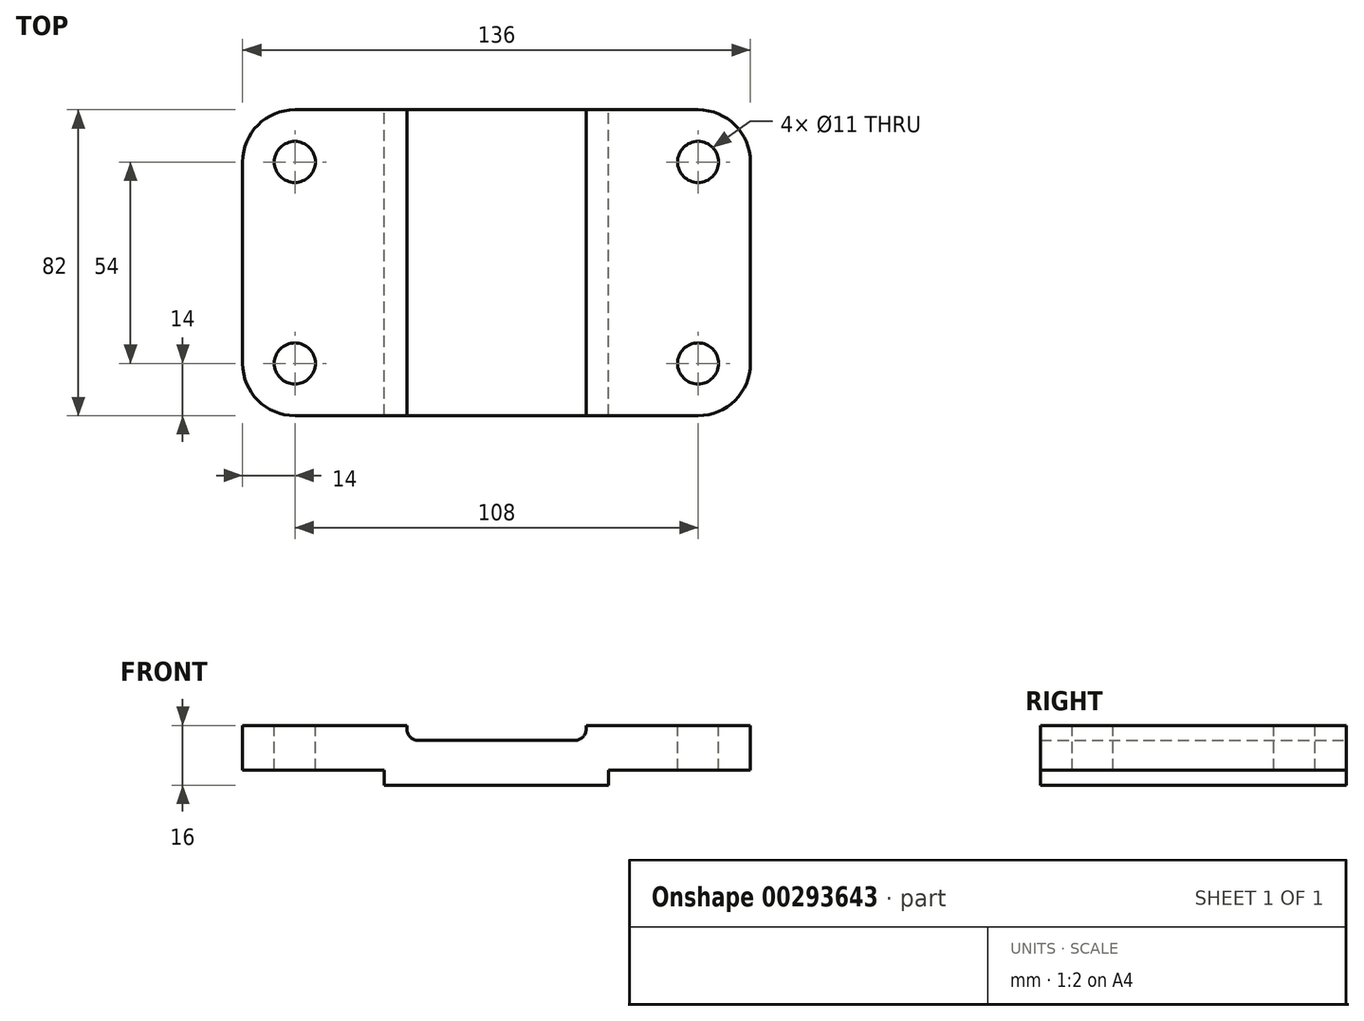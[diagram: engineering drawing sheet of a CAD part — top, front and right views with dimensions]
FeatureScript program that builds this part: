
annotation { "Feature Type Name" : "Feature", "Feature Type Description" : "" }
export const myFeature = defineFeature(function(context is Context, id is Id, definition is map)
    precondition{}
    {
        {
            var Q0;
            Q0=qCreatedBy(makeId("Front.planeOp"),FACE);
            var sketch = newSketch(context, id + "F0", { "sketchPlane" : qUnion([Q0])});
            skLineSegment(sketch, "E0", {"start": v(0, 0) * mm, "end": v(0, 4) * mm});
            skLineSegment(sketch, "E1", {"start": v(0, 4) * mm, "end": v(-38, 4) * mm});
            skLineSegment(sketch, "E2", {"start": v(-38, 4) * mm, "end": v(-38, 16) * mm});
            skLineSegment(sketch, "E3", {"start": v(-38, 16) * mm, "end": v(6, 16) * mm});
            skLineSegment(sketch, "E4", {"start": v(6, 16) * mm, "end": v(6, 15) * mm});
            skLineSegment(sketch, "E5", {"start": v(9, 12) * mm, "end": v(51, 12) * mm});
            skLineSegment(sketch, "E6", {"start": v(54, 15) * mm, "end": v(54, 16) * mm});
            skLineSegment(sketch, "E7", {"start": v(54, 16) * mm, "end": v(98, 16) * mm});
            skLineSegment(sketch, "E8", {"start": v(98, 16) * mm, "end": v(98, 4) * mm});
            skLineSegment(sketch, "E9", {"start": v(98, 4) * mm, "end": v(60, 4) * mm});
            skLineSegment(sketch, "E10", {"start": v(60, 4) * mm, "end": v(60, 0) * mm});
            skLineSegment(sketch, "E11", {"start": v(60, 0) * mm, "end": v(0, 0) * mm});
            skPoint(sketch, "E12.visualSharp", {"position": v(6, 12) * mm});
            skArc(sketch, "E12.filletArc", {"start": v(6, 15) * mm, "mid": v(6.88, 12.88) * mm, "end": v(9, 12) * mm});
            skPoint(sketch, "E13.visualSharp", {"position": v(54, 12) * mm});
            skArc(sketch, "E13.filletArc", {"start": v(51, 12) * mm, "mid": v(53.12, 12.88) * mm, "end": v(54, 15) * mm});
            skSolve(sketch);
        }
        {
            var Q0;
            Q0=makeQuery(id+"F0.imprint","IMPRINT",FACE,{"disambiguationData":[TD([[makeQuery(id+"F0.imprint","IMPRINT",EDGE,{"derivedFrom":sQuery(id+"F0.wireOp",EDGE,"E0")}),-1.0]])]});
            extrude(context, id + "F1", {"entities" : qUnion([Q0]), "depth" : 82 * mm});
        }
        {
            var Q0;
            Q0=makeQuery(id+"F1.opExtrude","CAP_EDGE",EDGE,{"disambiguationData":[OSD([sQuery(id+"F0.wireOp",EDGE,"E8")])],"isStart":false});
            var Q1;
            Q1=makeQuery(id+"F1.opExtrude","CAP_EDGE",EDGE,{"disambiguationData":[OSD([sQuery(id+"F0.wireOp",EDGE,"E8")])],"isStart":true});
            var Q2;
            Q2=makeQuery(id+"F1.opExtrude","CAP_EDGE",EDGE,{"disambiguationData":[OSD([sQuery(id+"F0.wireOp",EDGE,"E2")])],"isStart":true});
            var Q3;
            Q3=makeQuery(id+"F1.opExtrude","CAP_EDGE",EDGE,{"disambiguationData":[OSD([sQuery(id+"F0.wireOp",EDGE,"E2")])],"isStart":false});
            fillet(context, id + "F2", {"entities" : qUnion([Q0, Q1, Q2, Q3]), "radius" : 14 * mm, "tangentPropagation" : true, "allowEdgeOverflow" : false});
        }
        {
            var Q0;
            Q0=makeQuery(id+"F1.opExtrude","SWEPT_FACE",FACE,{"disambiguationData":[OSD([sQuery(id+"F0.wireOp",EDGE,"E3")])]});
            var sketch = newSketch(context, id + "F3", { "sketchPlane" : qUnion([Q0])});
            skLineSegment(sketch, "E14.0.0", {"start": v(6, 0) * mm, "end": v(-24, 0) * mm});
            skArc(sketch, "E14.0.1", {"start": v(-24, 0) * mm, "mid": v(-33.9, -4.1) * mm, "end": v(-38, -14) * mm});
            skLineSegment(sketch, "E14.0.2", {"start": v(-38, -14) * mm, "end": v(-38, -68) * mm});
            skArc(sketch, "E14.0.3", {"start": v(-38, -68) * mm, "mid": v(-33.9, -77.9) * mm, "end": v(-24, -82) * mm});
            skLineSegment(sketch, "E14.0.4", {"start": v(-24, -82) * mm, "end": v(6, -82) * mm});
            skLineSegment(sketch, "E14.0.5", {"start": v(6, -82) * mm, "end": v(6, 0) * mm});
            skCircle(sketch, "E15", {"center": v(-24, -14) * mm, "radius": 5.5 * mm});
            skCircle(sketch, "E16.0.1.0", {"center": v(-24, -68) * mm, "radius": 5.5 * mm});
            skCircle(sketch, "E16.1.0.0", {"center": v(84, -14) * mm, "radius": 5.5 * mm});
            skCircle(sketch, "E16.1.1.0", {"center": v(84, -68) * mm, "radius": 5.5 * mm});
            skLineSegment(sketch, "E16.direction1", {"start": v(-24, -14) * mm, "end": v(84, -14) * mm, "construction": true});
            skLineSegment(sketch, "E16.direction2", {"start": v(-24, -14) * mm, "end": v(-24, -68) * mm, "construction": true});
            skSolve(sketch);
        }
        {
            var Q0;
            Q0=makeQuery(id+"F3.imprint","IMPRINT",FACE,{"disambiguationData":[TD([[makeQuery(id+"F3.imprint","IMPRINT",EDGE,{"derivedFrom":sQuery(id+"F3.wireOp",EDGE,"E15")}),1.0]])]});
            var Q1;
            Q1=makeQuery(id+"F3.imprint","IMPRINT",FACE,{"disambiguationData":[TD([[makeQuery(id+"F3.imprint","IMPRINT",EDGE,{"derivedFrom":sQuery(id+"F3.wireOp",EDGE,"E16.0.1.0")}),1.0]])]});
            var Q2;
            Q2=makeQuery(id+"F3.imprint","IMPRINT",FACE,{"disambiguationData":[TD([[makeQuery(id+"F3.imprint","IMPRINT",EDGE,{"derivedFrom":sQuery(id+"F3.wireOp",EDGE,"E16.1.1.0")}),1.0]])]});
            var Q3;
            Q3=makeQuery(id+"F3.imprint","IMPRINT",FACE,{"disambiguationData":[TD([[makeQuery(id+"F3.imprint","IMPRINT",EDGE,{"derivedFrom":sQuery(id+"F3.wireOp",EDGE,"E16.1.0.0")}),1.0]])]});
            extrude(context, id + "F4", {"entities" : qUnion([Q0, Q1, Q2, Q3]), "operationType" : NewBodyOperationType.REMOVE, "oppositeDirection" : true, "depth" : 25 * mm});
        }
    });
